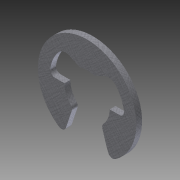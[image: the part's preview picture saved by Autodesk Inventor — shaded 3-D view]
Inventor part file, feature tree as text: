
AUTODESK INVENTOR PART (.ipt)
format: ipt  version: 2012 (Build 160160000, 160)  size: 129,536 bytes
history: native  units: in
note: dims shown in document units (in); Inventor stores cm internally (conversion verified against a paired STEP export)
features: fillet x2, extrude x1, sketch x1
ambient origin geometry x8: Origin, YZ Plane, XZ Plane, XY Plane, X Axis, Y Axis, Z Axis, Center Point
bodies: Solid1 (feature_tree)
feature tree (4):
  extrude  "Extrusion1"  Depth=0.303in
  fillet  "Fillet1"  Radius=0.5in
  fillet  "Fillet2"  Radius=0.039in
  sketch  "Sketch1"  dims[d0=0.66in d1=0.303in d2=0.5in d3=0.039in d4=0.0in d5=0.0625in d6=0.0312in]
